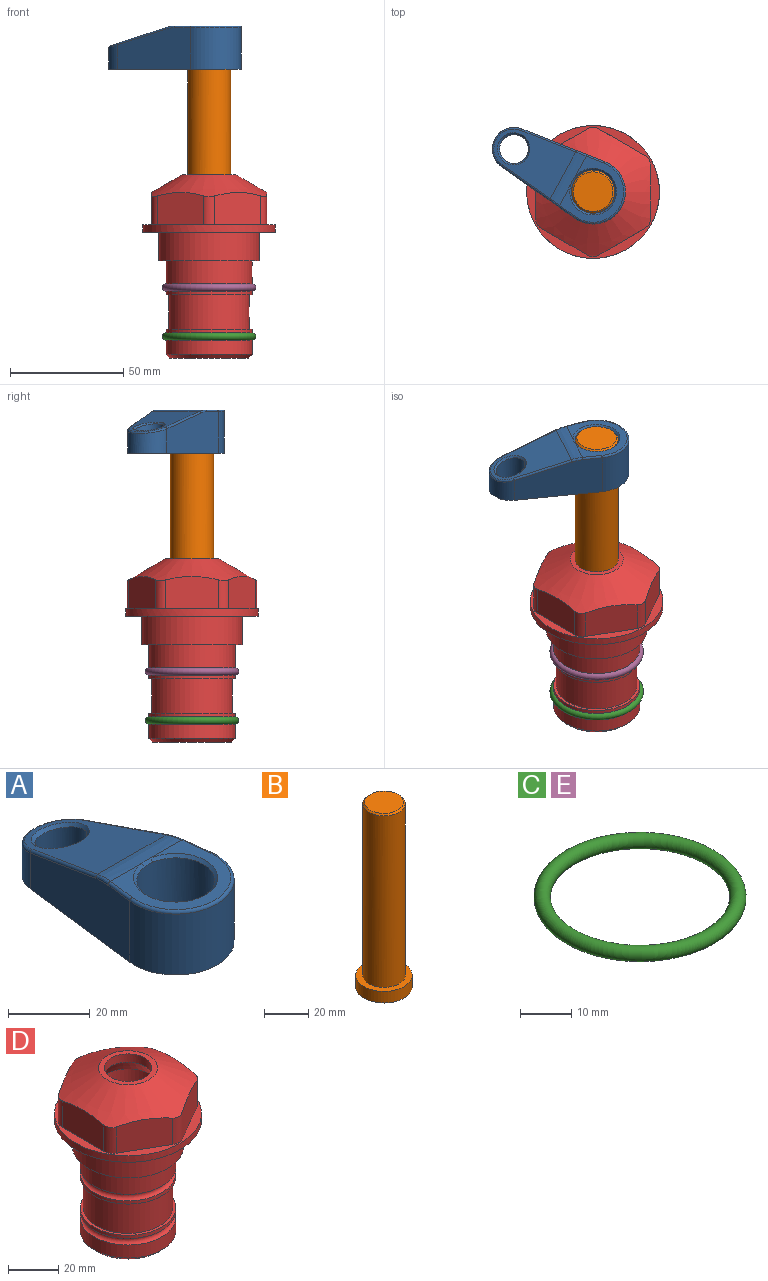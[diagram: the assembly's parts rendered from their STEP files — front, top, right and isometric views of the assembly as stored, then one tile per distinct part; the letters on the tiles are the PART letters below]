
ASSEMBLY  parts=5 mates=4
PART A: 31 faces, bbox 31.7x65.5x19.8 mm
  f0: plane 39.12x18.26mm, normal (0.99,0.12,0), area 612.2mm2, adj f1,f4,f7,f11,f13,f15
  f1: cylinder r=9.53mm len=18.91mm, axis (0,0,-1), area 296.1mm2, adj f0,f2,f7,f17
  f2: plane 39.12x18.26mm, normal (-0.99,0.12,0), area 612.2mm2, adj f1,f4,f7,f12,f14,f16
  f3: cylinder r=6.35mm len=12.7mm, axis (0,0,-1), area 362.4mm2, adj f7,f18
  f4: cylinder r=14.29mm len=28.58mm, axis (0,0,-1), area 882.2mm2, adj f0,f2,f7,f10
  f5: cylinder r=9.53mm len=19.05mm, axis (0,0,-1), area 1092.6mm2, adj f7,f19,f20
  f6: plane 26.99x23.69mm, normal (0,0,1), area 216.2mm2, adj f9,f10,f11,f12,f19
  f7: plane 63.5x28.58mm, normal (0,0,-1), area 661.8mm2, adj f0,f1,f2,f3,f4,f5,f22,f23
  f8: plane 33.52x23.6mm, normal (0,0.26,0.97), area 486mm2, adj f9,f15,f16,f17,f18
  f9: cylinder r=19.05mm len=24.72mm, axis (1,0,0), area 120.4mm2, adj f6,f8,f13,f14,f20
  f10: torus R=13.49mm, axis (0,0,1), area 59mm2, adj f4,f6,f11,f12
  f11: cylinder r=0.79mm len=8.67mm, axis (0.12,-0.99,0), area 10.8mm2, adj f0,f6,f10,f13
  f12: cylinder r=0.79mm len=8.67mm, axis (0.12,0.99,0), area 10.8mm2, adj f2,f6,f10,f14
  f13: bspline ~4.95x1.42mm, area 6.1mm2, adj f0,f9,f11,f15
  f14: bspline ~4.95x1.42mm, area 6.1mm2, adj f2,f9,f12,f16
  f15: cylinder r=0.79mm len=25.95mm, axis (0.12,-0.96,0.26), area 32.9mm2, adj f0,f8,f13,f17
  f16: cylinder r=0.79mm len=25.95mm, axis (0.12,0.96,-0.26), area 32.9mm2, adj f2,f8,f14,f17
  f17: bspline ~18.91x8.38mm, area 30mm2, adj f1,f8,f15,f16
  f18: bspline ~14.29x14.29mm, area 48.3mm2, adj f3,f8
  f19: cone r=9.53mm half-angle=45deg, axis (0,0,1), area 66.5mm2, adj f5,f6,f20
  f20: bspline ~3.22x0.96mm, area 3.5mm2, adj f5,f9,f19
  f21: plane 2.75x2.72mm, normal (0,0,-1), area 2.9mm2, adj f23,f25,f28
  f22: plane 23.05x15.88mm, normal (-0.99,-0.12,0), area 323.6mm2, adj f7,f25,f26,f27,f28,f29
  f23: plane 23.05x15.88mm, normal (0.99,-0.12,0), area 323.6mm2, adj f7,f21,f25,f27,f28,f30
  f24: cylinder r=9.53mm len=10.69mm, axis (0,0,-1), area 114.7mm2, adj f7,f27,f29,f30
  f25: cylinder r=12.7mm len=20.59mm, axis (0,0,-1), area 381.1mm2, adj f7,f21,f22,f23,f26,f28
  f26: plane 2.75x2.72mm, normal (0,0,-1), area 2.9mm2, adj f22,f25,f28
  f27: plane 19.72x18.37mm, normal (0,-0.26,-0.97), area 291.8mm2, adj f22,f23,f24,f28,f29,f30
  f28: cylinder r=15.88mm len=19.92mm, axis (1,0,0), area 54.8mm2, adj f21,f22,f23,f25,f26,f27
  f29: cylinder r=1.59mm len=11mm, axis (0,0,-1), area 34.7mm2, adj f7,f22,f24,f27
  f30: cylinder r=1.59mm len=11mm, axis (0,0,-1), area 34.7mm2, adj f7,f23,f24,f27
PART B: 6 faces, bbox 25.4x25.4x101.6 mm
  f0: plane 17.46x17.46mm, normal (0,0,1), area 239.5mm2, adj f5
  f1: plane 25.4x25.4mm, normal (0,0,-1), area 506.7mm2, adj f2
  f2: cylinder r=12.7mm len=25.4mm, axis (0,0,1), area 506.7mm2, adj f1,f3
  f3: plane 25.4x25.4mm, normal (0,0,1), area 221.7mm2, adj f2,f4
  f4: cylinder r=9.53mm len=94.46mm, axis (0,0,1), area 5653mm2, adj f3,f5
  f5: cone r=8.73mm half-angle=45deg, axis (0,0,-1), area 64.4mm2, adj f0,f4
PART C: 1 faces, bbox 44.7x44.7x3.2 mm
  f0: torus R=19.05mm, axis (0,0,1), area 1193.9mm2
PART D: 36 faces, bbox 58.7x58.7x81 mm
  f0: cylinder r=17.78mm len=35.56mm, axis (0,0,1), area 1670.8mm2, adj f23,f24,f31
  f1: cylinder r=19.05mm len=38.1mm, axis (0,0,1), area 1191.9mm2, adj f26,f27,f30
  f2: plane 58.66x58.66mm, normal (0,0,-1), area 1150.6mm2, adj f3,f28
  f3: cylinder r=29.33mm len=58.66mm, axis (0,0,-1), area 585.1mm2, adj f2,f4
  f4: plane 58.66x58.66mm, normal (0,0,1), area 475.9mm2, adj f3,f5,f6,f7,f8,f9,f10,f11
  f5: plane 20.32x14.34mm, normal (-0.5,0.87,0), area 324.4mm2, adj f4,f15,f16,f17
  f6: plane 20.32x14.34mm, normal (0.5,0.87,0), area 324.4mm2, adj f4,f14,f15,f17
  f7: plane 23.48x14.34mm, normal (1,0,0), area 324.4mm2, adj f4,f13,f14,f17
  f8: plane 20.32x14.34mm, normal (0.5,-0.87,0), area 324.4mm2, adj f4,f12,f13,f17
  f9: plane 20.32x14.34mm, normal (-0.5,-0.87,0), area 324.4mm2, adj f4,f11,f12,f17
  f10: plane 23.48x14.34mm, normal (-1,0,0), area 324.4mm2, adj f4,f11,f16,f17
  f11: cylinder r=5.08mm len=12.85mm, axis (0,0,-1), area 67.2mm2, adj f4,f9,f10,f17
  f12: cylinder r=5.08mm len=12.85mm, axis (0,0,-1), area 67.2mm2, adj f4,f8,f9,f17
  f13: cylinder r=5.08mm len=12.85mm, axis (0,0,-1), area 67.2mm2, adj f4,f7,f8,f17
  f14: cylinder r=5.08mm len=12.85mm, axis (0,0,-1), area 67.2mm2, adj f4,f6,f7,f17
  f15: cylinder r=5.08mm len=12.85mm, axis (0,0,-1), area 67.2mm2, adj f4,f5,f6,f17
  f16: cylinder r=5.08mm len=12.85mm, axis (0,0,-1), area 67.2mm2, adj f4,f5,f10,f17
  f17: cone r=11.73mm half-angle=60deg, axis (0,0,-1), area 2071.8mm2, adj f5,f6,f7,f8,f9,f10,f11,f12
  f18: plane 23.46x23.46mm, normal (0,0,1), area 147.4mm2, adj f17,f35
  f19: plane 34.93x34.93mm, normal (0,0,-1), area 958mm2, adj f29
  f20: cylinder r=19.05mm len=38.1mm, axis (0,0,1), area 760.1mm2, adj f21,f29
  f21: torus R=19.05mm, axis (0,0,1), area 565.3mm2, adj f20,f22
  f22: cylinder r=19.05mm len=38.1mm, axis (0,0,1), area 190mm2, adj f21,f23
  f23: plane 38.1x38.1mm, normal (0,0,1), area 146.9mm2, adj f0,f22
  f24: plane 38.1x38.1mm, normal (0,0,-1), area 146.9mm2, adj f0,f25
  f25: cylinder r=19.05mm len=38.1mm, axis (0,0,1), area 190mm2, adj f24,f26
  f26: torus R=19.05mm, axis (0,0,1), area 565.3mm2, adj f1,f25
  f27: plane 44.45x44.45mm, normal (0,0,-1), area 411.7mm2, adj f1,f28
  f28: cylinder r=22.23mm len=44.45mm, axis (0,0,1), area 1773.5mm2, adj f2,f27
  f29: cone r=19.05mm half-angle=45deg, axis (0,0,1), area 257.5mm2, adj f19,f20
  f30: cylinder r=3.17mm len=6.75mm, axis (-1,0,0), area 128mm2, adj f1,f33
  f31: cylinder r=3.17mm len=6.35mm, axis (-1,0,0), area 102.5mm2, adj f0,f33
  f32: plane 25.4x25.4mm, normal (0,0,1), area 506.7mm2, adj f33
  f33: cylinder r=12.7mm len=66.42mm, axis (0,0,-1), area 5236.2mm2, adj f30,f31,f32,f34
  f34: cone r=9.53mm half-angle=30deg, axis (0,0,-1), area 443.4mm2, adj f33,f35
  f35: cylinder r=9.53mm len=19.05mm, axis (0,0,-1), area 240.9mm2, adj f18,f34
PART E: same geometry as C
PLACE A rot(axis=(0,0,1),61.6deg) t=(0,0,27.55)mm
PLACE B rot(axis=(0,0,1),61.6deg) t=(0,0,27.55)mm
PLACE C t=(0,0,-21.59)mm
PLACE D at identity fixed
PLACE E at identity
MATE fastened E.f0 <-> D.f0  axis (0,0,1) through (0,0,-24.51)mm
MATE fastened B.f2 <-> A.f4  axis (0,0,1) through (0,0,91.05)mm
MATE fastened C.f0 <-> D.f0  axis (0,0,1) through (0,0,-46.1)mm
MATE cylindrical B.f2 <-> D.f0  axis (0,0,-1) through (0,0,-10.55)mm
